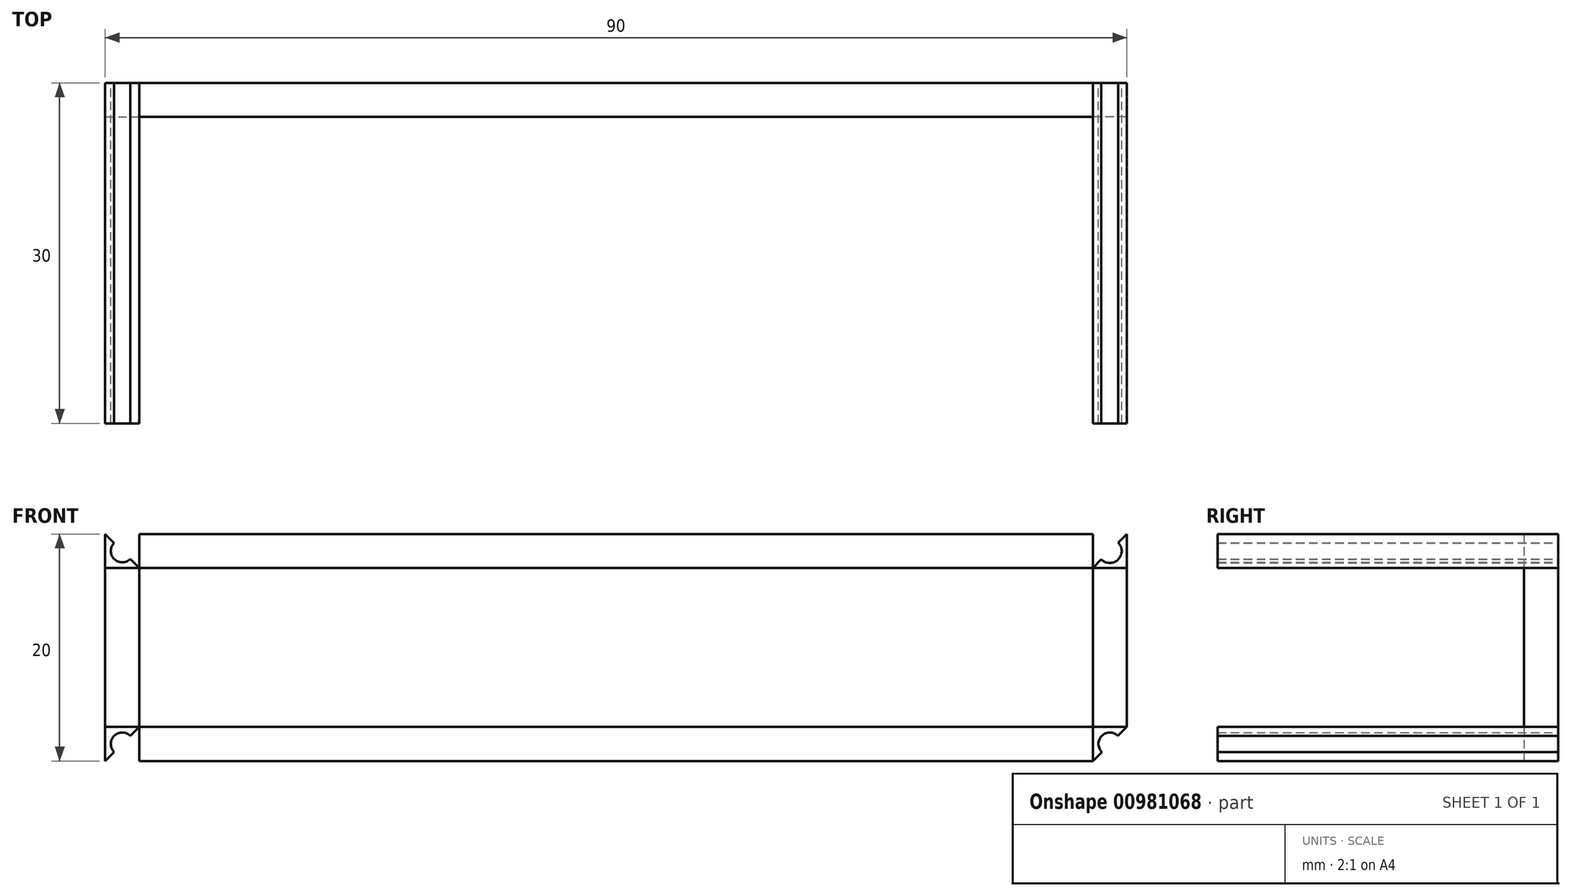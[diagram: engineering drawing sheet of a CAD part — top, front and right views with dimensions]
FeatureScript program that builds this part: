
annotation { "Feature Type Name" : "Feature", "Feature Type Description" : "" }
export const myFeature = defineFeature(function(context is Context, id is Id, definition is map)
    precondition{}
    {
        {
            var Q0;
            Q0=qCreatedBy(makeId("Front.planeOp"),FACE);
            var sketch = newSketch(context, id + "F0", { "sketchPlane" : qUnion([Q0])});
            skLineSegment(sketch, "E0.bottom", {"start": v(-42, 7) * mm, "end": v(42, 7) * mm});
            skLineSegment(sketch, "E0.top", {"start": v(-42, -7) * mm, "end": v(42, -7) * mm});
            skLineSegment(sketch, "E0.left", {"start": v(-42, 7) * mm, "end": v(-42, -7) * mm});
            skLineSegment(sketch, "E0.right", {"start": v(42, 7) * mm, "end": v(42, -7) * mm});
            skLineSegment(sketch, "E1.bottom", {"start": v(-45, 10) * mm, "end": v(45, 10) * mm});
            skLineSegment(sketch, "E1.top", {"start": v(-45, -10) * mm, "end": v(45, -10) * mm});
            skLineSegment(sketch, "E1.left", {"start": v(-45, 10) * mm, "end": v(-45, -10) * mm});
            skLineSegment(sketch, "E1.right", {"start": v(45, 10) * mm, "end": v(45, -10) * mm});
            skPoint(sketch, "E1.middle", {"position": v(0, 0) * mm});
            skLineSegment(sketch, "E2.bottom", {"start": v(-42, -7) * mm, "end": v(-45, -7) * mm});
            skLineSegment(sketch, "E2.top", {"start": v(-42, -10) * mm, "end": v(-45, -10) * mm});
            skLineSegment(sketch, "E2.left", {"start": v(-42, -7) * mm, "end": v(-42, -10) * mm});
            skLineSegment(sketch, "E2.right", {"start": v(-45, -7) * mm, "end": v(-45, -10) * mm});
            skLineSegment(sketch, "E3.bottom", {"start": v(42, -7) * mm, "end": v(45, -7) * mm});
            skLineSegment(sketch, "E3.top", {"start": v(42, -10) * mm, "end": v(45, -10) * mm});
            skLineSegment(sketch, "E3.left", {"start": v(42, -7) * mm, "end": v(42, -10) * mm});
            skLineSegment(sketch, "E3.right", {"start": v(45, -7) * mm, "end": v(45, -10) * mm});
            skLineSegment(sketch, "E4.bottom", {"start": v(45, 10) * mm, "end": v(-45, 10) * mm});
            skLineSegment(sketch, "E4.top", {"start": v(45, 10) * mm, "end": v(-45, 10) * mm});
            skLineSegment(sketch, "E4.left", {"start": v(45, 10) * mm, "end": v(45, 10) * mm});
            skLineSegment(sketch, "E4.right", {"start": v(-45, 10) * mm, "end": v(-45, 10) * mm});
            skLineSegment(sketch, "E5.bottom", {"start": v(-45, 10) * mm, "end": v(-42, 10) * mm});
            skLineSegment(sketch, "E5.top", {"start": v(-45, 7) * mm, "end": v(-42, 7) * mm});
            skLineSegment(sketch, "E5.left", {"start": v(-45, 10) * mm, "end": v(-45, 7) * mm});
            skLineSegment(sketch, "E5.right", {"start": v(-42, 10) * mm, "end": v(-42, 7) * mm});
            skLineSegment(sketch, "E6.bottom", {"start": v(45, 10) * mm, "end": v(42, 10) * mm});
            skLineSegment(sketch, "E6.top", {"start": v(45, 7) * mm, "end": v(42, 7) * mm});
            skLineSegment(sketch, "E6.left", {"start": v(45, 10) * mm, "end": v(45, 7) * mm});
            skLineSegment(sketch, "E6.right", {"start": v(42, 10) * mm, "end": v(42, 7) * mm});
            skLineSegment(sketch, "E7", {"start": v(45, 10) * mm, "end": v(42, 7) * mm});
            skCircle(sketch, "E8", {"center": v(43.5, 8.5) * mm, "radius": 1.05 * mm});
            skLineSegment(sketch, "E9", {"start": v(-45, 10) * mm, "end": v(-42, 7) * mm});
            skCircle(sketch, "E10", {"center": v(-43.5, 8.5) * mm, "radius": 1 * mm});
            skLineSegment(sketch, "E11", {"start": v(-42, -7) * mm, "end": v(-45, -10) * mm});
            skCircle(sketch, "E12", {"center": v(-43.5, -8.5) * mm, "radius": 1 * mm});
            skLineSegment(sketch, "E13", {"start": v(45, -7) * mm, "end": v(42, -10) * mm});
            skCircle(sketch, "E14", {"center": v(43.5, -8.5) * mm, "radius": 1 * mm});
            skSolve(sketch);
        }
        {
            var Q0;
            Q0=makeQuery(id+"F0.imprint","IMPRINT",FACE,{"disambiguationData":[TD([[makeQuery(id+"F0.imprint","IMPRINT",EDGE,{"derivedFrom":sQuery(id+"F0.wireOp",EDGE,"E0.bottom")}),1.0]])]});
            var Q1;
            Q1=makeQuery(id+"F0.imprint","IMPRINT",FACE,{"disambiguationData":[TD([[makeQuery(id+"F0.imprint","IMPRINT",EDGE,{"derivedFrom":sQuery(id+"F0.wireOp",EDGE,"E0.top")}),-1.0]])]});
            var Q2;
            Q2=makeQuery(id+"F0.imprint","IMPRINT",FACE,{"disambiguationData":[TD([[makeQuery(id+"F0.imprint","IMPRINT",EDGE,{"derivedFrom":sQuery(id+"F0.wireOp",EDGE,"E0.left")}),-1.0]])]});
            var Q3;
            Q3=makeQuery(id+"F0.imprint","IMPRINT",FACE,{"disambiguationData":[TD([[makeQuery(id+"F0.imprint","IMPRINT",EDGE,{"derivedFrom":sQuery(id+"F0.wireOp",EDGE,"E0.right")}),1.0]])]});
            extrude(context, id + "F1", {"entities" : qUnion([Q0, Q1, Q2, Q3]), "depth" : 3 * mm, "offsetDistance" : 25 * mm});
        }
        {
            var Q0;
            {var subQ1=sQuery(id+"F0.wireOp",EDGE,"E3.bottom");Q0=makeQuery(id+"F0.imprint","IMPRINT",FACE,{"disambiguationData":[TD([[makeQuery(id+"F0.imprint","IMPRINT",EDGE,{"derivedFrom":subQ1}),-1.0]])]});}
            var Q1;
            {var subQ1=sQuery(id+"F0.wireOp",EDGE,"E3.top");Q1=makeQuery(id+"F0.imprint","IMPRINT",FACE,{"disambiguationData":[TD([[makeQuery(id+"F0.imprint","IMPRINT",EDGE,{"derivedFrom":subQ1}),1.0]])]});}
            var Q2;
            {var subQ4=sQuery(id+"F0.wireOp",EDGE,"E2.bottom");Q2=makeQuery(id+"F0.imprint","IMPRINT",FACE,{"disambiguationData":[TD([[makeQuery(id+"F0.imprint","IMPRINT",EDGE,{"derivedFrom":subQ4}),1.0]])]});}
            var Q3;
            {var subQ1=sQuery(id+"F0.wireOp",EDGE,"E2.top");Q3=makeQuery(id+"F0.imprint","IMPRINT",FACE,{"disambiguationData":[TD([[makeQuery(id+"F0.imprint","IMPRINT",EDGE,{"derivedFrom":subQ1}),-1.0]])]});}
            var Q4;
            {var subQ1=sQuery(id+"F0.wireOp",EDGE,"E5.top");Q4=makeQuery(id+"F0.imprint","IMPRINT",FACE,{"disambiguationData":[TD([[makeQuery(id+"F0.imprint","IMPRINT",EDGE,{"derivedFrom":subQ1}),1.0]])]});}
            var Q5;
            {var subQ1=sQuery(id+"F0.wireOp",EDGE,"E5.bottom");Q5=makeQuery(id+"F0.imprint","IMPRINT",FACE,{"disambiguationData":[TD([[makeQuery(id+"F0.imprint","IMPRINT",EDGE,{"derivedFrom":subQ1}),-1.0]])]});}
            var Q6;
            {var subQ4=sQuery(id+"F0.wireOp",EDGE,"E6.bottom");Q6=makeQuery(id+"F0.imprint","IMPRINT",FACE,{"disambiguationData":[TD([[makeQuery(id+"F0.imprint","IMPRINT",EDGE,{"derivedFrom":subQ4}),1.0]])]});}
            var Q7;
            {var subQ4=sQuery(id+"F0.wireOp",EDGE,"E6.top");Q7=makeQuery(id+"F0.imprint","IMPRINT",FACE,{"disambiguationData":[TD([[makeQuery(id+"F0.imprint","IMPRINT",EDGE,{"derivedFrom":subQ4}),-1.0]])]});}
            extrude(context, id + "F2", {"entities" : qUnion([Q0, Q1, Q2, Q3, Q4, Q5, Q6, Q7]), "depth" : 30 * mm, "offsetDistance" : 25 * mm});
        }
    });
